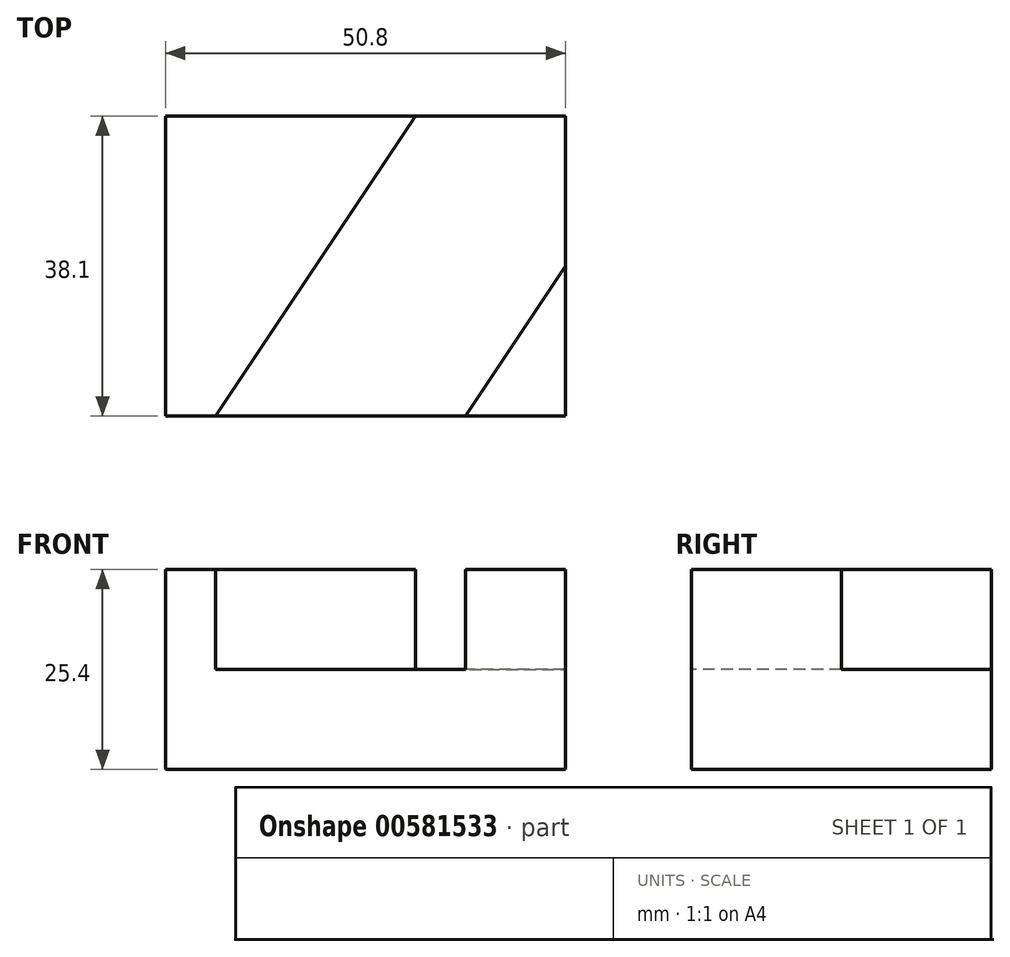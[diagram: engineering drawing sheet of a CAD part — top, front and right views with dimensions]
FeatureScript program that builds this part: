
annotation { "Feature Type Name" : "Feature", "Feature Type Description" : "" }
export const myFeature = defineFeature(function(context is Context, id is Id, definition is map)
    precondition{}
    {
        {
            var Q0;
            Q0=qCreatedBy(makeId("Top.planeOp"),FACE);
            var sketch = newSketch(context, id + "F0", { "sketchPlane" : qUnion([Q0])});
            skLineSegment(sketch, "E0", {"start": v(-63.02, 55.17) * mm, "end": v(-12.22, 55.17) * mm});
            skLineSegment(sketch, "E1", {"start": v(-12.22, 55.17) * mm, "end": v(-12.22, 17.07) * mm});
            skLineSegment(sketch, "E2", {"start": v(-12.22, 17.07) * mm, "end": v(-63.02, 17.07) * mm});
            skLineSegment(sketch, "E3", {"start": v(-63.02, 17.07) * mm, "end": v(-63.02, 55.17) * mm});
            skSolve(sketch);
        }
        {
            var Q0;
            Q0 = qSketchRegion(id + "F0", true);
            extrude(context, id + "F1", {"entities" : qUnion([Q0]), "depth" : 25.4 * mm, "offsetDistance" : 25.4 * mm});
        }
        {
            var Q0;
            Q0=makeQuery(id+"F1.opExtrude","CAP_FACE",FACE,{"disambiguationData":[OSD([sQuery(id+"F0.wireOp",EDGE,"E0"),sQuery(id+"F0.wireOp",EDGE,"E1"),sQuery(id+"F0.wireOp",EDGE,"E2"),sQuery(id+"F0.wireOp",EDGE,"E3")])],"isStart":false});
            var sketch = newSketch(context, id + "F2", { "sketchPlane" : qUnion([Q0])});
            skLineSegment(sketch, "E4", {"start": v(-31.27, 55.17) * mm, "end": v(-56.67, 17.07) * mm});
            skLineSegment(sketch, "E5", {"start": v(-56.67, 17.07) * mm, "end": v(-12.22, 17.07) * mm});
            skLineSegment(sketch, "E6", {"start": v(-12.22, 17.07) * mm, "end": v(-12.22, 55.17) * mm});
            skLineSegment(sketch, "E7", {"start": v(-12.22, 55.17) * mm, "end": v(-31.27, 55.17) * mm});
            skSolve(sketch);
        }
        {
            var Q0;
            Q0 = qSketchRegion(id + "F2", true);
            extrude(context, id + "F3", {"entities" : qUnion([Q0]), "operationType" : NewBodyOperationType.REMOVE, "oppositeDirection" : true, "depth" : 12.7 * mm, "offsetDistance" : 25.4 * mm});
        }
        {
            var Q0;
            Q0=makeQuery(id+"F3.boolean.opBoolean","COPY",FACE,{"derivedFrom":makeQuery(id+"F3.opExtrude","CAP_FACE",FACE,{"disambiguationData":[OSD([sQuery(id+"F2.wireOp",EDGE,"E4"),sQuery(id+"F2.wireOp",EDGE,"E5"),sQuery(id+"F2.wireOp",EDGE,"E6"),sQuery(id+"F2.wireOp",EDGE,"E7")])],"isStart":false})});
            var sketch = newSketch(context, id + "F4", { "sketchPlane" : qUnion([Q0])});
            skPoint(sketch, "E8.end.orphan", {"position": v(-12.22, 17.07) * mm});
            skPoint(sketch, "E9.start.orphan", {"position": v(-24.92, 17.07) * mm});
            skLineSegment(sketch, "E10", {"start": v(-12.22, 17.07) * mm, "end": v(-12.22, 36.12) * mm});
            skLineSegment(sketch, "E11", {"start": v(-12.22, 36.12) * mm, "end": v(-24.92, 17.07) * mm});
            skLineSegment(sketch, "E12", {"start": v(-24.92, 17.07) * mm, "end": v(-12.22, 17.07) * mm});
            skSolve(sketch);
        }
        {
            var Q0;
            Q0 = qSketchRegion(id + "F4", true);
            extrude(context, id + "F5", {"entities" : qUnion([Q0]), "operationType" : NewBodyOperationType.ADD, "depth" : 12.7 * mm, "offsetDistance" : 25.4 * mm});
        }
    });
